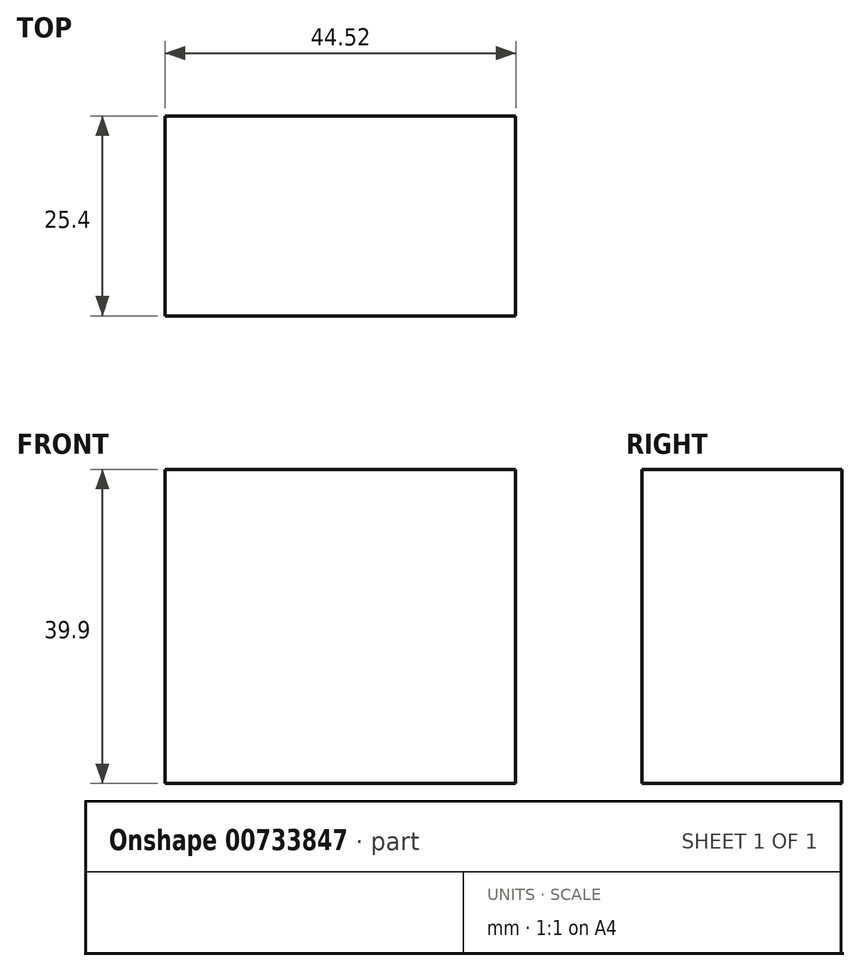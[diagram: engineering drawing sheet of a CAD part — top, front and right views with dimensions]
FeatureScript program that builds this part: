
annotation { "Feature Type Name" : "Feature", "Feature Type Description" : "" }
export const myFeature = defineFeature(function(context is Context, id is Id, definition is map)
    precondition{}
    {
        {
            var Q0;
            Q0=qCreatedBy(makeId("Front.planeOp"),FACE);
            var sketch = newSketch(context, id + "F0", { "sketchPlane" : qUnion([Q0])});
            skLineSegment(sketch, "E0.bottom", {"start": v(-11.28, 66.02) * mm, "end": v(38.65, 66.02) * mm});
            skLineSegment(sketch, "E0.top", {"start": v(-11.28, 16.2) * mm, "end": v(38.65, 16.2) * mm});
            skLineSegment(sketch, "E0.left", {"start": v(-11.28, 66.02) * mm, "end": v(-11.28, 16.2) * mm});
            skLineSegment(sketch, "E0.right", {"start": v(38.65, 66.02) * mm, "end": v(38.65, 16.2) * mm});
            skLineSegment(sketch, "E1", {"start": v(38.65, 66.02) * mm, "end": v(33.24, 56.1) * mm});
            skLineSegment(sketch, "E2", {"start": v(33.24, 56.1) * mm, "end": v(33.24, 6.82) * mm});
            skLineSegment(sketch, "E3", {"start": v(38.65, 16.2) * mm, "end": v(33.24, 6.82) * mm});
            skLineSegment(sketch, "E4", {"start": v(-11.28, 66.02) * mm, "end": v(-16.7, 56.1) * mm});
            skLineSegment(sketch, "E5", {"start": v(33.24, 56.1) * mm, "end": v(-16.7, 56.1) * mm});
            skLineSegment(sketch, "E6", {"start": v(-16.7, 56.1) * mm, "end": v(-16.7, 7.07) * mm});
            skLineSegment(sketch, "E7", {"start": v(-16.7, 7.07) * mm, "end": v(-11.28, 16.2) * mm});
            skLineSegment(sketch, "E8", {"start": v(-16.7, 7.07) * mm, "end": v(33.24, 6.82) * mm});
            skSolve(sketch);
        }
        {
            var Q0;
            {var subQ1=sQuery(id+"F0.wireOp",EDGE,"E0.top");var subQ3=sQuery(id+"F0.wireOp",EDGE,"E2");var subQ4=makeQuery(id+"F0.imprint","INTERSECT",VERTEX,{"derivedFrom":[subQ1,subQ3]});Q0=makeQuery(id+"F0.imprint","IMPRINT",FACE,{"disambiguationData":[TD([[makeQuery(id+"F0.imprint","IMPRINT",EDGE,{"disambiguationData":[TD([[subQ4,1.0]])],"derivedFrom":subQ1}),1.0]])]});}
            extrude(context, id + "F1", {"entities" : qUnion([Q0]), "depth" : 25.4 * mm, "offsetDistance" : 25.4 * mm});
        }
    });
